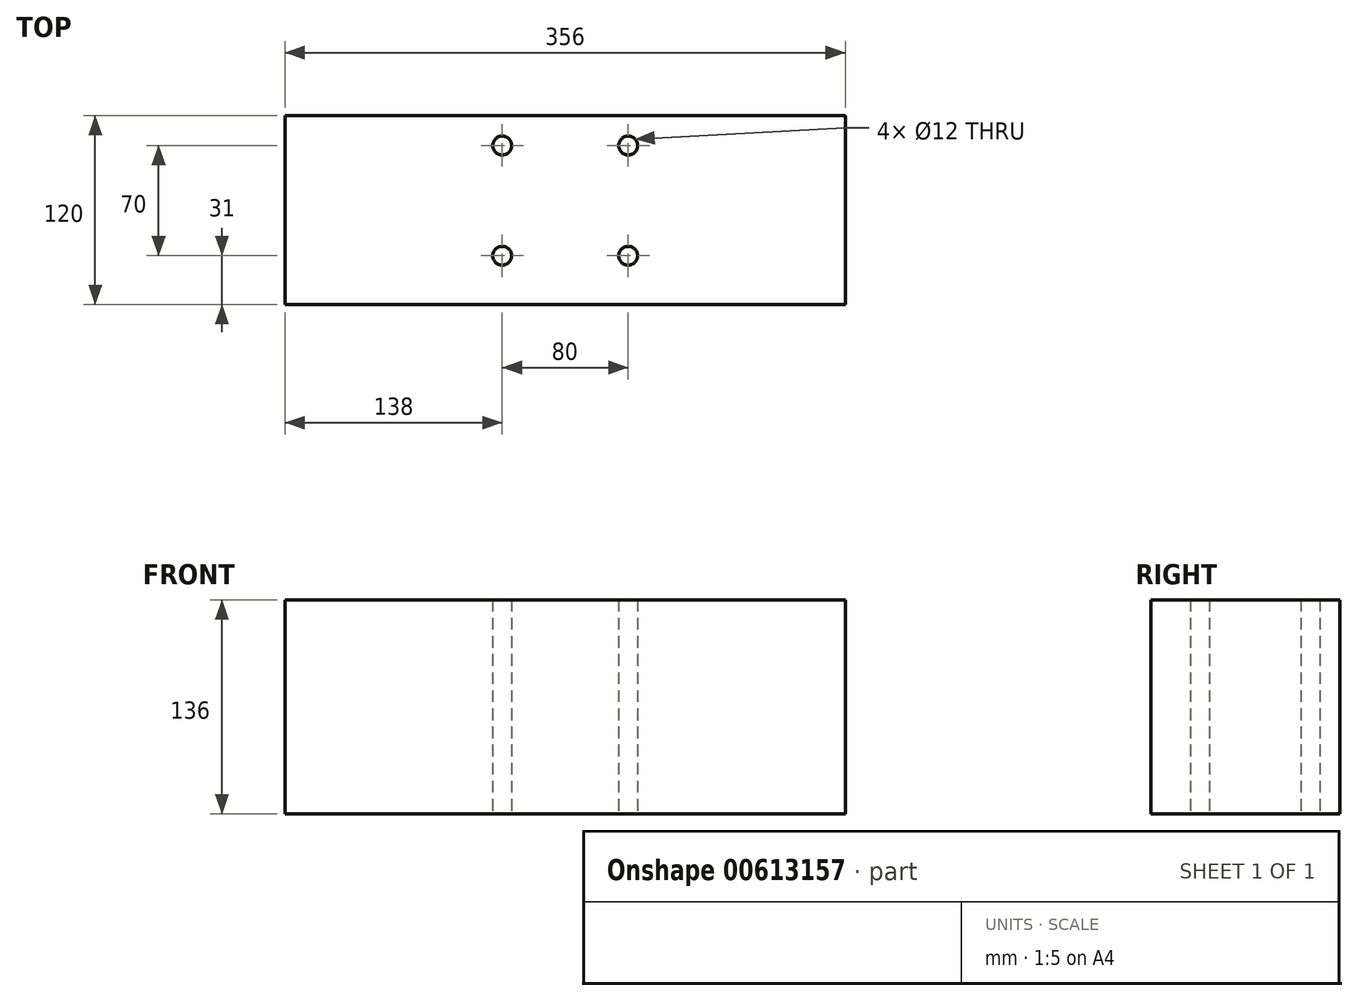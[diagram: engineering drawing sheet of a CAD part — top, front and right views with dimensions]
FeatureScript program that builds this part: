
annotation { "Feature Type Name" : "Feature", "Feature Type Description" : "" }
export const myFeature = defineFeature(function(context is Context, id is Id, definition is map)
    precondition{}
    {
        {
            var Q0;
            Q0=qCreatedBy(makeId("Top.planeOp"),FACE);
            var sketch = newSketch(context, id + "F0", { "sketchPlane" : qUnion([Q0])});
            skLineSegment(sketch, "E0.bottom", {"start": v(178, 60) * mm, "end": v(-178, 60) * mm});
            skLineSegment(sketch, "E0.top", {"start": v(178, -60) * mm, "end": v(-178, -60) * mm});
            skLineSegment(sketch, "E0.left", {"start": v(178, 60) * mm, "end": v(178, -60) * mm});
            skLineSegment(sketch, "E0.right", {"start": v(-178, 60) * mm, "end": v(-178, -60) * mm});
            skPoint(sketch, "E0.middle", {"position": v(0, 0) * mm});
            skCircle(sketch, "E1", {"center": v(-40, 41) * mm, "radius": 6 * mm});
            skCircle(sketch, "E2", {"center": v(40, 41) * mm, "radius": 6 * mm});
            skCircle(sketch, "E3", {"center": v(40, -29) * mm, "radius": 6 * mm});
            skCircle(sketch, "E4", {"center": v(-40, -29) * mm, "radius": 6 * mm});
            skSolve(sketch);
        }
        {
            var Q0;
            Q0=makeQuery(id+"F0.imprint","IMPRINT",FACE,{"disambiguationData":[TD([[makeQuery(id+"F0.imprint","IMPRINT",EDGE,{"derivedFrom":sQuery(id+"F0.wireOp",EDGE,"E0.bottom")}),1.0]])]});
            extrude(context, id + "F1", {"entities" : qUnion([Q0]), "depth" : 136 * mm, "offsetDistance" : 25 * mm});
        }
    });
